# Revit family: Lighting - Luminii - Kurba Medium Dome Horizontal - Array
name_source: partatom
category: Lighting Fixtures
units: mm (PartAtom-declared; Revit-internal decimal feet)

## family parameters
Cut with Voids When Loaded = No
Host = Face
Light Source = No
OmniClass Number = 23.80.70.11.14.21
OmniClass Title = Spots and Tracklight Specialties
Part Type = Normal
Room Calculation Point = No
Round Connector Dimension = Use Diameter
Shared = Yes

## types (1)
- Kurba Medium Dome Horizontal
    Apparent Load = 4 VA
    Assembly Code = D5020230
    CCT = 3000K
    Current Amps = 0 A
    Default Elevation = 0 "
    Depth = 1 "
    Description = Flexible LED Strip
    Environment = Wet
    Finish = Metal - Luminii - Silver Anodized Aluminum
    Frequency = 60 Hz
    Has Battery Backup = No
    Has Dimming = No
    Housing Protection Rating = IP20 Dry/IP66 Wet Series
    Initial Color Comments = Perfomance based on 3500K Photometric Web File
    Instruction Sheet Link = https://www.luminii.com
    Keynote = 26 50 00
    Lamp = LED
    Lamp Life = 1
    Lens Material = Plastic - Luminii - Frosted Lens
    Load Classification = Lighting
    Lumen Output = 134 lm/ft
    Manufacturer = Luminii
    Model = KBM-D-H
    Mounting Method = Surface Mount
    Number of Poles = 1
    Operating Temperature = -4°F-113°F
    Phase = 1
    Power Factor = 1
    Power Source Type = Driver
    Product Documentation Link = https://www.luminii.com
    Product Name = Kurba Medium Dome Horizontal
    Product Page URL = https://www.luminii.com
    URL = https://www.luminii.com
    Version = 2020 - v1.0a
    Voltage = 120 V
    Voltage Comments = 120-277VAC
    Warranty URL = https://www.luminii.com
    Wattage Comments = 3.7 W/ft
    Width = 1 "

## geometry (parser evidence)
native form markers: Sweep x3
no freeform markers — native parametric forms only
